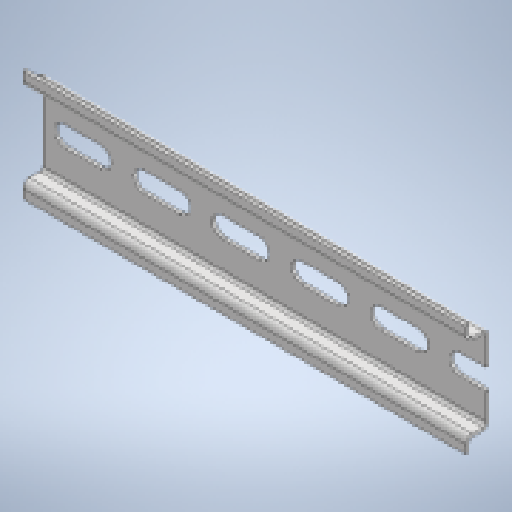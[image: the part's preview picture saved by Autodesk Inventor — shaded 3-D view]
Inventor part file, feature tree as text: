
AUTODESK INVENTOR PART (.ipt)
format: ipt  version: 2023 (Build 270158030, 158C)  size: 393,728 bytes
history: native  units: mm
features: other x4, extrude x3, sketch x3, reference x1
ambient origin geometry x8: Origin, YZ Plane, XZ Plane, XY Plane, X Axis, Y Axis, Z Axis, Center Point
bodies: Body1 (feature_tree)
feature tree (11):
  other  "DIN"
  extrude  "Extrusion1"  Depth=1.0mm
  extrude  "Extrusion2"  Depth=7.3mm
  extrude  "Extrusion3"  Depth=1.0mm
  sketch  "Sketch1"  dims[d0=1.0mm d1=1.0mm]
  reference  "Reference1"
  sketch  "Sketch2"  dims[d5=35.0mm d8=7.3mm]
  sketch  "Sketch3"  dims[d9=1.0mm d10=1.0mm d11=2.0mm d12=2.0mm d13=12.7mm d15=12.7mm d16=4.8mm d17=4.8mm d20=1.0mm d21=1.0mm d22=2.0mm d23=300.0mm d24=0.0mm d26=18.0mm d31=80.0mm d33=25.0mm d34=10.0mm d36=10.0mm d39=25.0mm d40=0.0mm d46=3.6mm d47=17.5mm d48=17.5mm d49=50.0mm d51=25.0mm d52=10.0mm d54=10.0mm d56=140.0mm d57=2.0mm d58=5.0mm d59=5.0mm d60=0.0mm d61=0.0mm]
  other  "<userpath>\Documents\0004-inventor\Inventor_Projects\electronics-enclosure\enclosure.iam"
  other  "enclosure.iam"
  other  "assembly-board:1"
